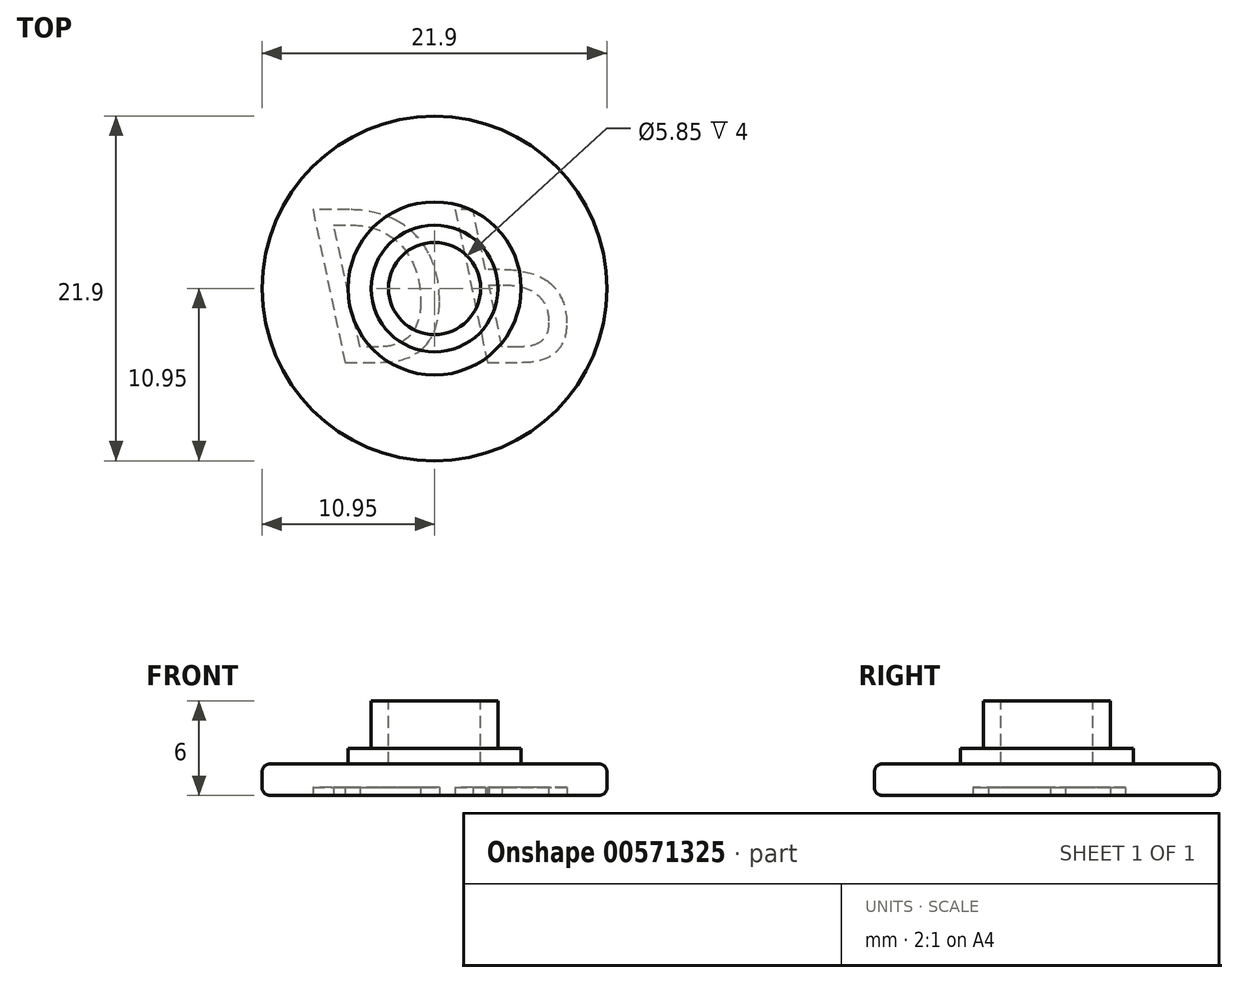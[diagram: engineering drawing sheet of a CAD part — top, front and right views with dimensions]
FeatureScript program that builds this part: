
annotation { "Feature Type Name" : "Feature", "Feature Type Description" : "" }
export const myFeature = defineFeature(function(context is Context, id is Id, definition is map)
    precondition{}
    {
        {
            var Q0;
            Q0=qCreatedBy(makeId("Top.planeOp"),FACE);
            var sketch = newSketch(context, id + "F0", { "sketchPlane" : qUnion([Q0])});
            skCircle(sketch, "E0", {"center": v(0, 0) * mm, "radius": 0.07 * mm});
            skCircle(sketch, "E1", {"center": v(0, 0) * mm, "radius": 10.95 * mm});
            skSolve(sketch);
        }
        {
            var Q0;
            Q0=qCreatedBy(makeId("Top.planeOp"),FACE);
            var sketch = newSketch(context, id + "F1", { "sketchPlane" : qUnion([Q0])});
            skCircle(sketch, "E2", {"center": v(0, 0) * mm, "radius": 5.5 * mm});
            skSolve(sketch);
        }
        {
            var Q0;
            Q0=qCreatedBy(makeId("Top.planeOp"),FACE);
            var sketch = newSketch(context, id + "F2", { "sketchPlane" : qUnion([Q0])});
            skCircle(sketch, "E3", {"center": v(0, 0) * mm, "radius": 4.03 * mm});
            skSolve(sketch);
        }
        {
            var Q0;
            Q0=qSketchRegion(id+"F0",true);
            extrude(context, id + "F3", {"entities" : qUnion([Q0]), "depth" : 2 * mm, "offsetDistance" : 25 * mm});
        }
        {
            var Q0;
            Q0=qSketchRegion(id+"F1",true);
            extrude(context, id + "F4", {"entities" : qUnion([Q0]), "operationType" : NewBodyOperationType.ADD, "depth" : 3 * mm});
        }
        {
            var Q0;
            Q0=qSketchRegion(id+"F2",true);
            extrude(context, id + "F5", {"entities" : qUnion([Q0]), "operationType" : NewBodyOperationType.ADD, "depth" : 6 * mm});
        }
        {
            var Q0;
            Q0=makeQuery(id+"F3.opExtrude","SWEPT_FACE",FACE,{"disambiguationData":[OSD([sQuery(id+"F0.wireOp",EDGE,"E1")])]});
            fillet(context, id + "F6", {"entities" : qUnion([Q0]), "radius" : .5 * mm, "tangentPropagation" : true, "allowEdgeOverflow" : false});
        }
        {
            var Q0;
            Q0=makeQuery(id+"F5.opExtrude","CAP_FACE",FACE,{"disambiguationData":[OSD([sQuery(id+"F2.wireOp",EDGE,"E3")])],"isStart":false});
            var sketch = newSketch(context, id + "F7", { "sketchPlane" : qUnion([Q0])});
            skCircle(sketch, "E4.0", {"center": v(0, 0) * mm, "radius": 2.92 * mm});
            skSolve(sketch);
        }
        {
            var Q0;
            Q0=qSketchRegion(id+"F7",true);
            extrude(context, id + "F8", {"entities" : qUnion([Q0]), "operationType" : NewBodyOperationType.REMOVE, "oppositeDirection" : true, "depth" : 4 * mm});
        }
        {
            var Q0;
            Q0=makeQuery(id+"F4.boolean.opBoolean","MERGE",FACE,{"derivedFrom":[makeQuery(id+"F3.opExtrude","CAP_FACE",FACE,{"disambiguationData":[OSD([sQuery(id+"F0.wireOp",EDGE,"E0"),sQuery(id+"F0.wireOp",EDGE,"E1")])],"isStart":true}),makeQuery(id+"F4.opExtrude","CAP_FACE",FACE,{"disambiguationData":[OSD([sQuery(id+"F1.wireOp",EDGE,"E2")])],"isStart":true})]});
            var sketch = newSketch(context, id + "F9", { "sketchPlane" : qUnion([Q0])});
            skText(sketch, "E5", { "text": "DP", "fontName": "OpenSans-Italic.ttf"});
            const initialGuessF9  = {"E5": [-0.0083, -0.005, 1, 0, 0.00977]};
            skSetInitialGuess(sketch, initialGuessF9);
            skSolve(sketch);
        }
        {
            var Q0;
            Q0 = qSketchRegion(id + "F9", true);
            extrude(context, id + "F10", {"entities" : qUnion([Q0]), "operationType" : NewBodyOperationType.REMOVE, "oppositeDirection" : true, "depth" : .5 * mm, "offsetDistance" : 25 * mm});
        }
    });
